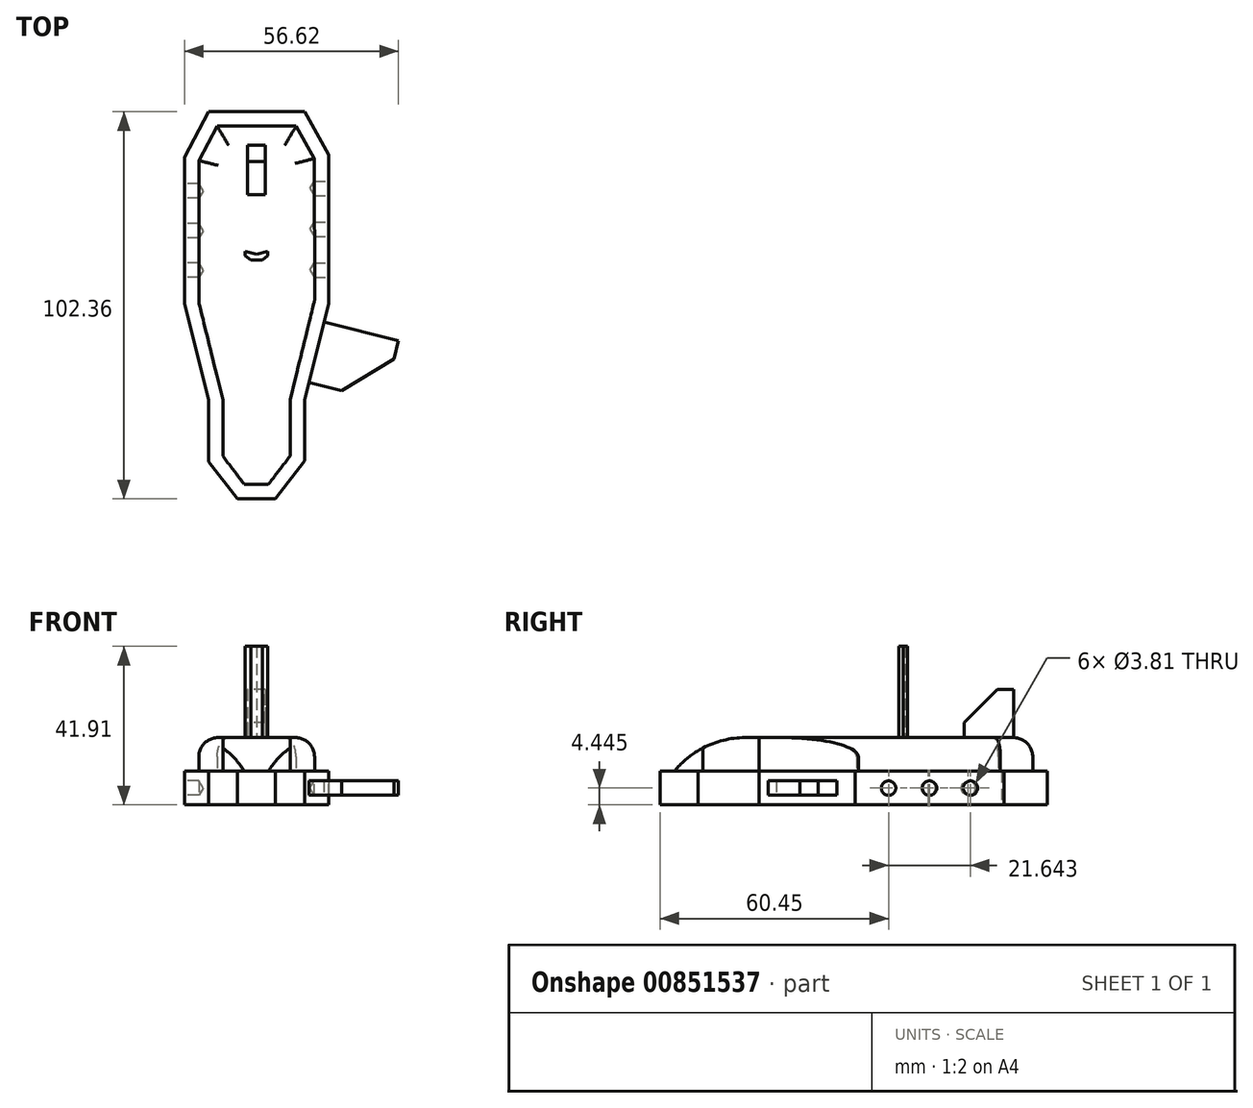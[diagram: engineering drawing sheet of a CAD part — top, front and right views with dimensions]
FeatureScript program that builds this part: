
annotation { "Feature Type Name" : "Feature", "Feature Type Description" : "" }
export const myFeature = defineFeature(function(context is Context, id is Id, definition is map)
    precondition{}
    {
        {
            var Q0;
            Q0=qCreatedBy(makeId("Top.planeOp"),FACE);
            var sketch = newSketch(context, id + "F0", { "sketchPlane" : qUnion([Q0])});
            skLineSegment(sketch, "E0.bottom", {"start": v(12.7, 38.1) * mm, "end": v(-12.7, 38.1) * mm});
            skLineSegment(sketch, "E0.left", {"start": v(19.05, 26.72) * mm, "end": v(19.05, -12.7) * mm});
            skLineSegment(sketch, "E0.right", {"start": v(-19.05, 26.13) * mm, "end": v(-19.05, -12.7) * mm});
            skPoint(sketch, "E0.middle", {"position": v(0, 0) * mm});
            skLineSegment(sketch, "E1.bottom", {"start": v(5.04, -64.26) * mm, "end": v(-5.09, -64.26) * mm});
            skLineSegment(sketch, "E1.left", {"start": v(12.7, -54.22) * mm, "end": v(12.7, -38.1) * mm});
            skLineSegment(sketch, "E1.right", {"start": v(-12.7, -54.45) * mm, "end": v(-12.7, -38.1) * mm});
            skPoint(sketch, "E1.middle", {"position": v(0, -38.1) * mm});
            skPoint(sketch, "E2", {"position": v(12.7, -38.1) * mm});
            skPoint(sketch, "E3", {"position": v(-12.7, -38.1) * mm});
            skPoint(sketch, "E4", {"position": v(0, -64.26) * mm});
            skPoint(sketch, "E5", {"position": v(-19.05, 0) * mm});
            skPoint(sketch, "E6", {"position": v(19.05, 0) * mm});
            skLineSegment(sketch, "E7", {"start": v(-12.7, -54.45) * mm, "end": v(-5.09, -64.26) * mm});
            skLineSegment(sketch, "E8", {"start": v(5.04, -64.26) * mm, "end": v(12.7, -54.22) * mm});
            skLineSegment(sketch, "E9", {"start": v(-19.05, -12.7) * mm, "end": v(-12.7, -38.1) * mm});
            skLineSegment(sketch, "E10", {"start": v(12.7, -38.1) * mm, "end": v(19.05, -12.7) * mm});
            skLineSegment(sketch, "E11", {"start": v(-12.7, 38.1) * mm, "end": v(-19.05, 26.13) * mm});
            skLineSegment(sketch, "E12", {"start": v(12.7, 38.1) * mm, "end": v(19.05, 26.72) * mm});
            skSolve(sketch);
        }
        {
            var Q0;
            Q0=makeQuery(id+"F0.imprint","IMPRINT",FACE,{"disambiguationData":[TD([[makeQuery(id+"F0.imprint","IMPRINT",EDGE,{"derivedFrom":sQuery(id+"F0.wireOp",EDGE,"E0.bottom")}),1.0]])]});
            extrude(context, id + "F1", {"entities" : qUnion([Q0]), "depth" : 8.9 * mm, "offsetDistance" : 25.4 * mm});
        }
        {
            var Q0;
            Q0=makeQuery(id+"F1.opExtrude","CAP_FACE",FACE,{"disambiguationData":[OSD([sQuery(id+"F0.wireOp",EDGE,"E0.bottom"),sQuery(id+"F0.wireOp",EDGE,"E0.left"),sQuery(id+"F0.wireOp",EDGE,"E0.right"),sQuery(id+"F0.wireOp",EDGE,"E1.bottom"),sQuery(id+"F0.wireOp",EDGE,"E1.left"),sQuery(id+"F0.wireOp",EDGE,"E1.right"),sQuery(id+"F0.wireOp",EDGE,"E7"),sQuery(id+"F0.wireOp",EDGE,"E8"),sQuery(id+"F0.wireOp",EDGE,"E9"),sQuery(id+"F0.wireOp",EDGE,"E10"),sQuery(id+"F0.wireOp",EDGE,"E11"),sQuery(id+"F0.wireOp",EDGE,"E12")])],"isStart":false});
            var sketch = newSketch(context, id + "F2", { "sketchPlane" : qUnion([Q0])});
            skPoint(sketch, "E13", {"position": v(-0.02, -60.45) * mm});
            skPoint(sketch, "E13.positionSnap0", {"position": v(-0.02, -64.26) * mm});
            skPoint(sketch, "E14", {"position": v(-8.89, -52.94) * mm});
            skPoint(sketch, "E15", {"position": v(8.9, -52.94) * mm});
            skPoint(sketch, "E16", {"position": v(3.16, -60.45) * mm});
            skPoint(sketch, "E17", {"position": v(-3.22, -60.45) * mm});
            skPoint(sketch, "E18", {"position": v(-8.89, -38.1) * mm});
            skPoint(sketch, "E19", {"position": v(8.9, -38.1) * mm});
            skLineSegment(sketch, "E20", {"start": v(-8.89, -38.1) * mm, "end": v(-8.89, -52.94) * mm});
            skLineSegment(sketch, "E21", {"start": v(-8.89, -38.1) * mm, "end": v(8.9, -38.1) * mm});
            skLineSegment(sketch, "E22", {"start": v(-8.89, -52.94) * mm, "end": v(-3.22, -60.45) * mm});
            skLineSegment(sketch, "E23", {"start": v(-0.02, -60.45) * mm, "end": v(3.16, -60.45) * mm});
            skLineSegment(sketch, "E24", {"start": v(-3.22, -60.45) * mm, "end": v(-0.02, -60.45) * mm});
            skLineSegment(sketch, "E25", {"start": v(3.16, -60.45) * mm, "end": v(8.9, -52.94) * mm});
            skLineSegment(sketch, "E26", {"start": v(8.9, -38.1) * mm, "end": v(8.9, -52.94) * mm});
            skPoint(sketch, "E27", {"position": v(-15.24, -12.23) * mm});
            skPoint(sketch, "E28", {"position": v(-15.24, 25.18) * mm});
            skPoint(sketch, "E29", {"position": v(-10.4, 34.3) * mm});
            skPoint(sketch, "E30", {"position": v(10.46, 34.3) * mm});
            skPoint(sketch, "E31", {"position": v(15.24, 25.73) * mm});
            skPoint(sketch, "E32", {"position": v(15.35, -11.78) * mm});
            skLineSegment(sketch, "E33", {"start": v(10.46, 34.3) * mm, "end": v(-10.4, 34.3) * mm});
            skLineSegment(sketch, "E34", {"start": v(-15.24, 25.18) * mm, "end": v(-10.4, 34.3) * mm});
            skLineSegment(sketch, "E35", {"start": v(-15.24, -12.23) * mm, "end": v(-15.24, 25.18) * mm});
            skLineSegment(sketch, "E36", {"start": v(-15.24, -12.23) * mm, "end": v(-8.89, -38.1) * mm});
            skLineSegment(sketch, "E37", {"start": v(8.9, -38.1) * mm, "end": v(15.35, -11.78) * mm});
            skLineSegment(sketch, "E38", {"start": v(15.24, 25.73) * mm, "end": v(15.35, -11.78) * mm});
            skLineSegment(sketch, "E39", {"start": v(15.24, 25.73) * mm, "end": v(10.46, 34.3) * mm});
            skSolve(sketch);
        }
        {
            var Q0;
            Q0=makeQuery(id+"F2.imprint","IMPRINT",FACE,{"disambiguationData":[TD([[makeQuery(id+"F2.imprint","IMPRINT",EDGE,{"derivedFrom":sQuery(id+"F2.wireOp",EDGE,"E20")}),1.0]])]});
            extrude(context, id + "F3", {"entities" : qUnion([Q0]), "depth" : 8.9 * mm, "offsetDistance" : 25.4 * mm});
        }
        {
            var Q0;
            Q0=makeQuery(id+"F3.opExtrude","CAP_EDGE",EDGE,{"disambiguationData":[OSD([sQuery(id+"F2.wireOp",EDGE,"E23"),sQuery(id+"F2.wireOp",EDGE,"E24")])],"isStart":false});
            fillet(context, id + "F4", {"entities" : qUnion([Q0]), "radius" : 24.13 * mm, "tangentPropagation" : true, "allowEdgeOverflow" : false});
        }
        {
            var Q0;
            Q0=makeQuery(id+"F2.imprint","IMPRINT",FACE,{"disambiguationData":[TD([[makeQuery(id+"F2.imprint","IMPRINT",EDGE,{"derivedFrom":sQuery(id+"F2.wireOp",EDGE,"E21")}),1.0]])]});
            extrude(context, id + "F5", {"entities" : qUnion([Q0]), "operationType" : NewBodyOperationType.ADD, "depth" : 8.9 * mm, "offsetDistance" : 25.4 * mm});
        }
        {
            var Q0;
            Q0=makeQuery(id+"F5.opExtrude","CAP_EDGE",EDGE,{"disambiguationData":[OSD([sQuery(id+"F2.wireOp",EDGE,"E35")])],"isStart":false});
            var Q1;
            Q1=makeQuery(id+"F5.opExtrude","CAP_EDGE",EDGE,{"disambiguationData":[OSD([sQuery(id+"F2.wireOp",EDGE,"E38")])],"isStart":false});
            var Q2;
            Q2=makeQuery(id+"F5.opExtrude","CAP_EDGE",EDGE,{"disambiguationData":[OSD([sQuery(id+"F2.wireOp",EDGE,"E34")])],"isStart":false});
            var Q3;
            Q3=makeQuery(id+"F5.opExtrude","CAP_EDGE",EDGE,{"disambiguationData":[OSD([sQuery(id+"F2.wireOp",EDGE,"E39")])],"isStart":false});
            var Q4;
            Q4=makeQuery(id+"F5.opExtrude","CAP_EDGE",EDGE,{"disambiguationData":[OSD([sQuery(id+"F2.wireOp",EDGE,"E33")])],"isStart":false});
            fillet(context, id + "F6", {"entities" : qUnion([Q0, Q1, Q2, Q3, Q4]), "radius" : 5.08 * mm, "tangentPropagation" : true, "allowEdgeOverflow" : false});
        }
        {
            var Q0;
            Q0=makeQuery(id+"F1.opExtrude","SWEPT_FACE",FACE,{"disambiguationData":[OSD([sQuery(id+"F0.wireOp",EDGE,"E0.left")])]});
            var sketch = newSketch(context, id + "F7", { "sketchPlane" : qUnion([Q0])});
            skPoint(sketch, "E40", {"position": v(7.01, 4.44) * mm});
            skPoint(sketch, "E41", {"position": v(17.83, 4.44) * mm});
            skPoint(sketch, "E42", {"position": v(-3.8, 4.44) * mm});
            skSolve(sketch);
        }
        {
            var Q0;
            Q0=sQuery(id+"F7.wireOp",VERTEX,"E42");
            var Q1;
            Q1=sQuery(id+"F7.wireOp",VERTEX,"E40");
            var Q2;
            Q2=sQuery(id+"F7.wireOp",VERTEX,"E41");
            var Q3;
            Q3=makeQuery(id+"F1.opExtrude","SWEPT_BODY",BODY,{"disambiguationData":[OSD([sQuery(id+"F0.wireOp",EDGE,"E0.bottom"),sQuery(id+"F0.wireOp",EDGE,"E0.left"),sQuery(id+"F0.wireOp",EDGE,"E0.right"),sQuery(id+"F0.wireOp",EDGE,"E1.bottom"),sQuery(id+"F0.wireOp",EDGE,"E1.left"),sQuery(id+"F0.wireOp",EDGE,"E1.right"),sQuery(id+"F0.wireOp",EDGE,"E7"),sQuery(id+"F0.wireOp",EDGE,"E8"),sQuery(id+"F0.wireOp",EDGE,"E9"),sQuery(id+"F0.wireOp",EDGE,"E10"),sQuery(id+"F0.wireOp",EDGE,"E11"),sQuery(id+"F0.wireOp",EDGE,"E12")])]});
            hole(context, id + "F8", {"style" : HoleStyle.SIMPLE, "endStyle" : HoleEndStyle.BLIND, "holeDiameter" : 3.8 * mm, "majorDiameter" : 19.05 * mm, "holeDepth" : 3.8 * mm, "isTappedThrough" : true, "tappedDepth" : 12.7 * mm, "tapClearance" : 3, "locations" : qUnion([Q0, Q1, Q2]), "scope" : qUnion([Q3])});
        }
        {
            var Q0;
            Q0=makeQuery(id+"F1.opExtrude","SWEPT_FACE",FACE,{"disambiguationData":[OSD([sQuery(id+"F0.wireOp",EDGE,"E0.right")])]});
            var sketch = newSketch(context, id + "F9", { "sketchPlane" : qUnion([Q0])});
            skPoint(sketch, "E43", {"position": v(-6.71, 8.9) * mm});
            skPoint(sketch, "E44", {"position": v(-6.68, 4.44) * mm});
            skPoint(sketch, "E45", {"position": v(3.8, 4.45) * mm});
            skPoint(sketch, "E46", {"position": v(-17.24, 4.44) * mm});
            skSolve(sketch);
        }
        {
            var Q0;
            Q0=sQuery(id+"F9.wireOp",VERTEX,"E46");
            var Q1;
            Q1=sQuery(id+"F9.wireOp",VERTEX,"E44");
            var Q2;
            Q2=sQuery(id+"F9.wireOp",VERTEX,"E45");
            var Q3;
            Q3=makeQuery(id+"F1.opExtrude","SWEPT_BODY",BODY,{"disambiguationData":[OSD([sQuery(id+"F0.wireOp",EDGE,"E0.bottom"),sQuery(id+"F0.wireOp",EDGE,"E0.left"),sQuery(id+"F0.wireOp",EDGE,"E0.right"),sQuery(id+"F0.wireOp",EDGE,"E1.bottom"),sQuery(id+"F0.wireOp",EDGE,"E1.left"),sQuery(id+"F0.wireOp",EDGE,"E1.right"),sQuery(id+"F0.wireOp",EDGE,"E7"),sQuery(id+"F0.wireOp",EDGE,"E8"),sQuery(id+"F0.wireOp",EDGE,"E9"),sQuery(id+"F0.wireOp",EDGE,"E10"),sQuery(id+"F0.wireOp",EDGE,"E11"),sQuery(id+"F0.wireOp",EDGE,"E12")])]});
            hole(context, id + "F10", {"style" : HoleStyle.SIMPLE, "endStyle" : HoleEndStyle.BLIND, "holeDiameter" : 3.8 * mm, "majorDiameter" : 6.35 * mm, "holeDepth" : 3.8 * mm, "isTappedThrough" : true, "tappedDepth" : 12.7 * mm, "tapClearance" : 3, "locations" : qUnion([Q0, Q1, Q2]), "scope" : qUnion([Q3])});
        }
        {
            var Q0;
            Q0=qCreatedBy(makeId("Top.planeOp"),FACE);
            var sketch = newSketch(context, id + "F11", { "sketchPlane" : qUnion([Q0])});
            skCircle(sketch, "E47", {"center": v(0, 0) * mm, "radius": 1.9 * mm});
            skSolve(sketch);
        }
        {
            var Q0;
            Q0=makeQuery(id+"F11.imprint","IMPRINT",FACE,{"disambiguationData":[TD([[makeQuery(id+"F11.imprint","IMPRINT",EDGE,{"derivedFrom":sQuery(id+"F11.wireOp",EDGE,"E47")}),1.0]])]});
            extrude(context, id + "F12", {"entities" : qUnion([Q0]), "depth" : 3.8 * mm, "offsetDistance" : 25.4 * mm});
        }
        {
            var Q0;
            Q0=makeQuery(id+"F12.opExtrude","CAP_FACE",FACE,{"disambiguationData":[OSD([sQuery(id+"F11.wireOp",EDGE,"E47")])],"isStart":false});
            var sketch = newSketch(context, id + "F13", { "sketchPlane" : qUnion([Q0])});
            skLineSegment(sketch, "E48.top", {"start": v(1.54, -1.13) * mm, "end": v(-1.54, -1.13) * mm});
            skLineSegment(sketch, "E48.left", {"start": v(3, 1.13) * mm, "end": v(3, 0) * mm});
            skLineSegment(sketch, "E48.right", {"start": v(-3, 1.13) * mm, "end": v(-3, 0) * mm});
            skPoint(sketch, "E48.middle", {"position": v(0, 0) * mm});
            skLineSegment(sketch, "E49", {"start": v(0, -1.13) * mm, "end": v(0, -1.9) * mm});
            skPoint(sketch, "E50", {"position": v(0, 0.45) * mm});
            skLineSegment(sketch, "E51", {"start": v(-3, 0) * mm, "end": v(-1.54, -1.13) * mm});
            skLineSegment(sketch, "E52", {"start": v(3, 0) * mm, "end": v(1.54, -1.13) * mm});
            skLineSegment(sketch, "E53", {"start": v(-3, 1.13) * mm, "end": v(0, 0.45) * mm});
            skLineSegment(sketch, "E54", {"start": v(3, 1.13) * mm, "end": v(0, 0.45) * mm});
            skSolve(sketch);
        }
        {
            var Q0;
            {var subQ0=sQuery(id+"F13.wireOp",EDGE,"E54");var subQ1=sQuery(id+"F13.wireOp",EDGE,"E53");var subQ2=makeQuery(id+"F13.imprint","INTERSECT",VERTEX,{"derivedFrom":[subQ1,subQ0]});Q0=makeQuery(id+"F13.imprint","IMPRINT",FACE,{"disambiguationData":[TD([[makeQuery(id+"F13.imprint","IMPRINT",EDGE,{"disambiguationData":[TD([[subQ2,1.0]])],"derivedFrom":subQ1}),-1.0]])]});}
            extrude(context, id + "F14", {"entities" : qUnion([Q0]), "operationType" : NewBodyOperationType.ADD, "depth" : 38.1 * mm, "offsetDistance" : 25.4 * mm});
        }
        {
            var Q0;
            {var subQ0=sQuery(id+"F13.wireOp",EDGE,"E48.right");Q0=makeQuery(id+"F13.imprint","IMPRINT",FACE,{"disambiguationData":[TD([[makeQuery(id+"F13.imprint","IMPRINT",EDGE,{"derivedFrom":subQ0}),1.0]])]});}
            extrude(context, id + "F15", {"entities" : qUnion([Q0]), "operationType" : NewBodyOperationType.ADD, "depth" : 38.1 * mm, "offsetDistance" : 25.4 * mm});
        }
        {
            var Q0;
            {var subQ0=sQuery(id+"F13.wireOp",EDGE,"E48.left");Q0=makeQuery(id+"F13.imprint","IMPRINT",FACE,{"disambiguationData":[TD([[makeQuery(id+"F13.imprint","IMPRINT",EDGE,{"derivedFrom":subQ0}),-1.0]])]});}
            extrude(context, id + "F16", {"entities" : qUnion([Q0]), "operationType" : NewBodyOperationType.ADD, "depth" : 38.1 * mm, "offsetDistance" : 25.4 * mm});
        }
        {
            var Q0;
            Q0=makeQuery(id+"F5.opExtrude","CAP_FACE",FACE,{"disambiguationData":[OSD([sQuery(id+"F2.wireOp",EDGE,"E21"),sQuery(id+"F2.wireOp",EDGE,"E33"),sQuery(id+"F2.wireOp",EDGE,"E34"),sQuery(id+"F2.wireOp",EDGE,"E35"),sQuery(id+"F2.wireOp",EDGE,"E36"),sQuery(id+"F2.wireOp",EDGE,"E37"),sQuery(id+"F2.wireOp",EDGE,"E38"),sQuery(id+"F2.wireOp",EDGE,"E39")])],"isStart":false});
            var sketch = newSketch(context, id + "F17", { "sketchPlane" : qUnion([Q0])});
            skPoint(sketch, "E55", {"position": v(0, 26.67) * mm});
            skLineSegment(sketch, "E56.bottom", {"start": v(2.34, 16.22) * mm, "end": v(-2.34, 16.22) * mm});
            skLineSegment(sketch, "E56.left", {"start": v(2.34, 16.22) * mm, "end": v(2.34, 29.2) * mm});
            skLineSegment(sketch, "E56.right", {"start": v(-2.34, 16.22) * mm, "end": v(-2.34, 29.2) * mm});
            skPoint(sketch, "E57", {"position": v(-2.34, 29.2) * mm});
            skPoint(sketch, "E58", {"position": v(2.34, 29.2) * mm});
            skLineSegment(sketch, "E59", {"start": v(-2.34, 29.2) * mm, "end": v(2.34, 29.2) * mm});
            skSolve(sketch);
        }
        {
            var Q0;
            Q0=makeQuery(id+"F17.imprint","IMPRINT",FACE,{"disambiguationData":[TD([[makeQuery(id+"F17.imprint","IMPRINT",EDGE,{"derivedFrom":sQuery(id+"F17.wireOp",EDGE,"E56.bottom")}),-1.0]])]});
            extrude(context, id + "F18", {"entities" : qUnion([Q0]), "depth" : 12.7 * mm, "offsetDistance" : 25.4 * mm});
        }
        {
            var Q0;
            Q0=makeQuery(id+"F18.opExtrude","CAP_EDGE",EDGE,{"disambiguationData":[OSD([sQuery(id+"F17.wireOp",EDGE,"E56.bottom")])],"isStart":false});
            chamfer(context, id + "F19", {"entities" : qUnion([Q0]), "width" : 8.76 * mm, "tangentPropagation" : true});
        }
        {
            var Q0;
            Q0=makeQuery(id+"F1.opExtrude","SWEPT_FACE",FACE,{"disambiguationData":[OSD([sQuery(id+"F0.wireOp",EDGE,"E10")])]});
            var sketch = newSketch(context, id + "F20", { "sketchPlane" : qUnion([Q0])});
            skPoint(sketch, "E60", {"position": v(-20.86, 4.45) * mm});
            skLineSegment(sketch, "E61.bottom", {"start": v(-12.6, 6.35) * mm, "end": v(-29.11, 6.35) * mm});
            skLineSegment(sketch, "E61.top", {"start": v(-12.6, 2.54) * mm, "end": v(-29.11, 2.54) * mm});
            skLineSegment(sketch, "E61.left", {"start": v(-12.6, 6.35) * mm, "end": v(-12.6, 2.54) * mm});
            skLineSegment(sketch, "E61.right", {"start": v(-29.11, 6.35) * mm, "end": v(-29.11, 2.54) * mm});
            skSolve(sketch);
        }
        {
            var Q0;
            Q0=makeQuery(id+"F20.imprint","IMPRINT",FACE,{"disambiguationData":[TD([[makeQuery(id+"F20.imprint","IMPRINT",EDGE,{"derivedFrom":sQuery(id+"F20.wireOp",EDGE,"E61.bottom")}),1.0]])]});
            extrude(context, id + "F21", {"entities" : qUnion([Q0]), "depth" : 20.32 * mm, "offsetDistance" : 25.4 * mm});
        }
        {
            var Q0;
            Q0=makeQuery(id+"F21.opExtrude","CAP_EDGE",EDGE,{"disambiguationData":[OSD([sQuery(id+"F20.wireOp",EDGE,"E61.right")])],"isStart":false});
            chamfer(context, id + "F22", {"entities" : qUnion([Q0]), "width" : 11.43 * mm, "tangentPropagation" : true});
        }
    });
